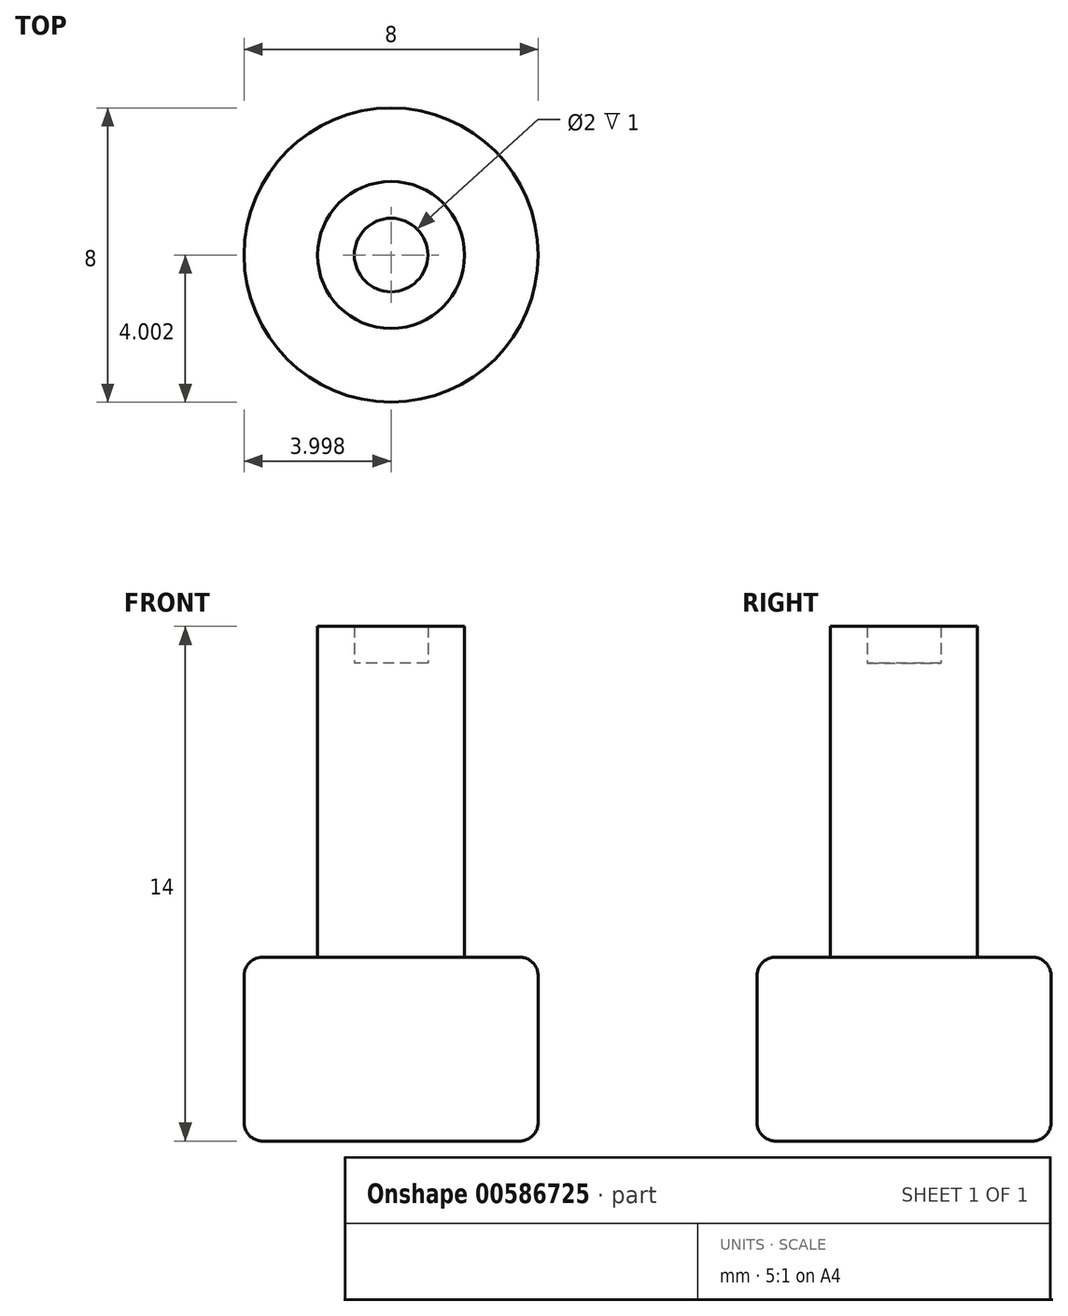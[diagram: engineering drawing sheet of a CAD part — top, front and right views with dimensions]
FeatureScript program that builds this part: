
annotation { "Feature Type Name" : "Feature", "Feature Type Description" : "" }
export const myFeature = defineFeature(function(context is Context, id is Id, definition is map)
    precondition{}
    {
        {
            var Q0;
            Q0=qCreatedBy(makeId("Top.planeOp"),FACE);
            var sketch = newSketch(context, id + "F0", { "sketchPlane" : qUnion([Q0])});
            skCircle(sketch, "E0", {"center": v(4.46, -9.28) * mm, "radius": 4 * mm});
            skSolve(sketch);
        }
        {
            var Q0;
            Q0=makeQuery(id+"F0.imprint","IMPRINT",FACE,{"disambiguationData":[TD([[makeQuery(id+"F0.imprint","IMPRINT",EDGE,{"derivedFrom":sQuery(id+"F0.wireOp",EDGE,"E0")}),1.0]])]});
            extrude(context, id + "F1", {"entities" : qUnion([Q0]), "depth" : 5 * mm, "offsetDistance" : 25 * mm});
        }
        {
            var Q0;
            Q0=makeQuery(id+"F1.opExtrude","CAP_FACE",FACE,{"disambiguationData":[OSD([sQuery(id+"F0.wireOp",EDGE,"E0")])],"isStart":false});
            var sketch = newSketch(context, id + "F2", { "sketchPlane" : qUnion([Q0])});
            skCircle(sketch, "E1", {"center": v(4.46, -9.28) * mm, "radius": 2 * mm});
            skSolve(sketch);
        }
        {
            var Q0;
            Q0=makeQuery(id+"F2.imprint","IMPRINT",FACE,{"disambiguationData":[TD([[makeQuery(id+"F2.imprint","IMPRINT",EDGE,{"derivedFrom":sQuery(id+"F2.wireOp",EDGE,"E1")}),1.0]])]});
            extrude(context, id + "F3", {"entities" : qUnion([Q0]), "operationType" : NewBodyOperationType.ADD, "depth" : 8 * mm, "offsetDistance" : 25 * mm});
        }
        {
            var Q0;
            Q0=makeQuery(id+"F3.opExtrude","CAP_FACE",FACE,{"disambiguationData":[OSD([sQuery(id+"F2.wireOp",EDGE,"E1")])],"isStart":false});
            var sketch = newSketch(context, id + "F4", { "sketchPlane" : qUnion([Q0])});
            skCircle(sketch, "E2", {"center": v(4.46, -9.28) * mm, "radius": 1 * mm});
            skSolve(sketch);
        }
        {
            var Q0;
            Q0=makeQuery(id+"F4.imprint","IMPRINT",FACE,{"disambiguationData":[TD([[makeQuery(id+"F4.imprint","IMPRINT",EDGE,{"derivedFrom":sQuery(id+"F4.wireOp",EDGE,"E2")}),-1.0]])]});
            extrude(context, id + "F5", {"entities" : qUnion([Q0]), "operationType" : NewBodyOperationType.ADD, "depth" : mm, "offsetDistance" : 25 * mm});
        }
        {
            var Q0;
            Q0=makeQuery(id+"F1.opExtrude","CAP_EDGE",EDGE,{"disambiguationData":[OSD([sQuery(id+"F0.wireOp",EDGE,"E0")])],"isStart":false});
            fillet(context, id + "F6", {"entities" : qUnion([Q0]), "radius" : 0.5 * mm, "tangentPropagation" : true, "allowEdgeOverflow" : false});
        }
        {
            var Q0;
            Q0=makeQuery(id+"F1.opExtrude","CAP_EDGE",EDGE,{"disambiguationData":[OSD([sQuery(id+"F0.wireOp",EDGE,"E0")])],"isStart":true});
            fillet(context, id + "F7", {"entities" : qUnion([Q0]), "radius" : 0.5 * mm, "tangentPropagation" : true, "allowEdgeOverflow" : false});
        }
    });
